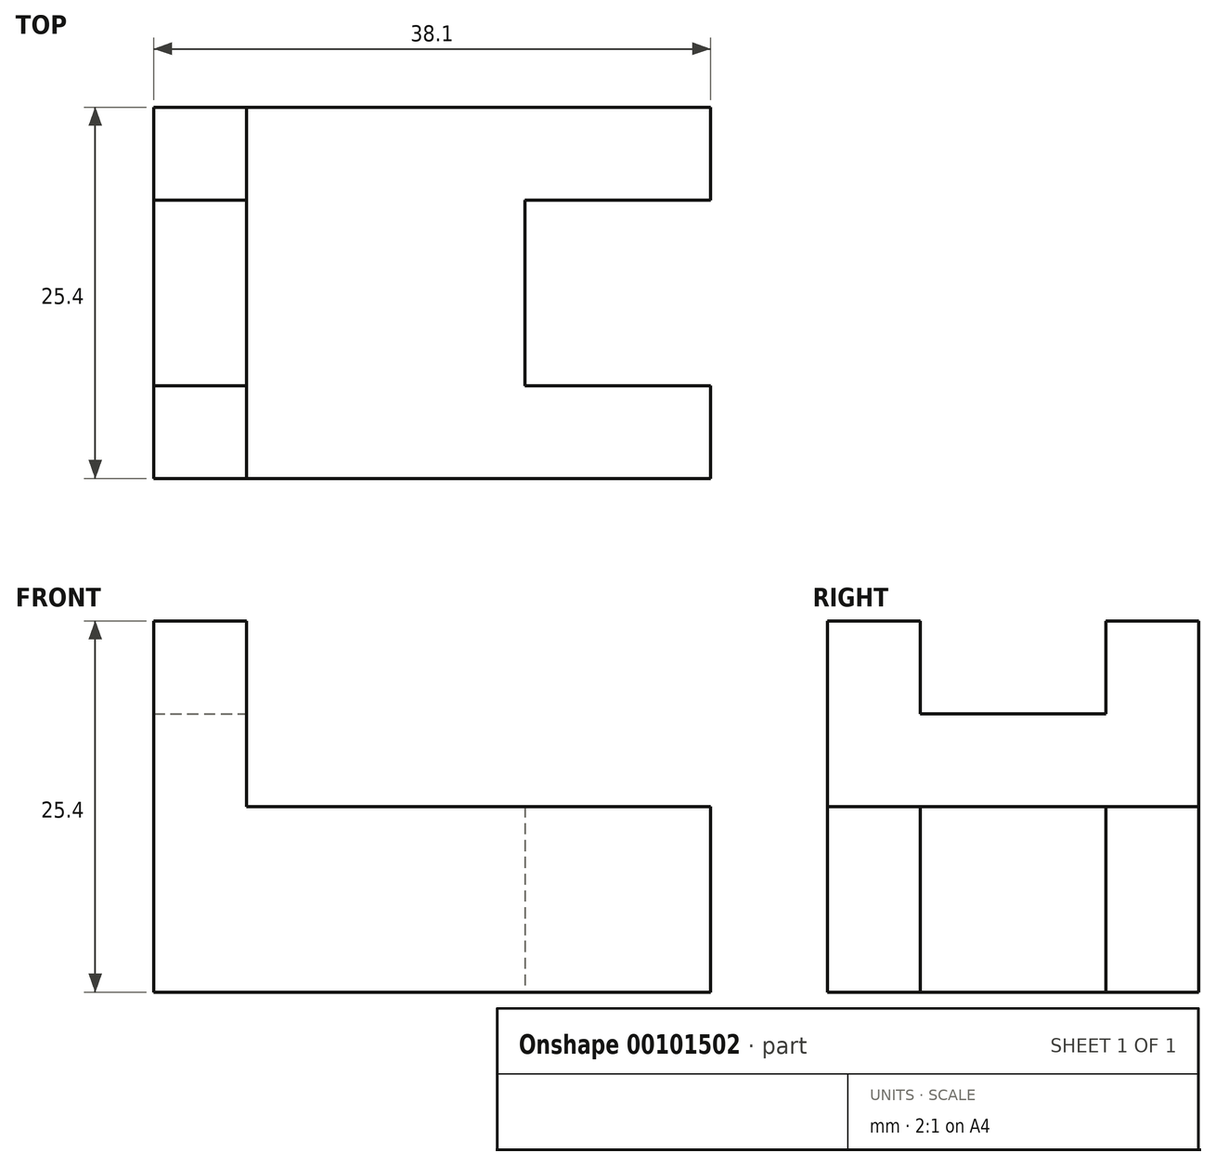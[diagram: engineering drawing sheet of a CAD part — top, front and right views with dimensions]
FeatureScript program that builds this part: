
annotation { "Feature Type Name" : "Feature", "Feature Type Description" : "" }
export const myFeature = defineFeature(function(context is Context, id is Id, definition is map)
    precondition{}
    {
        {
            var Q0;
            Q0=qCreatedBy(makeId("Front.planeOp"),FACE);
            var sketch = newSketch(context, id + "F0", { "sketchPlane" : qUnion([Q0])});
            skLineSegment(sketch, "E0", {"start": v(0, 0) * mm, "end": v(0, 25.4) * mm});
            skLineSegment(sketch, "E1", {"start": v(0, 25.4) * mm, "end": v(6.35, 25.4) * mm});
            skLineSegment(sketch, "E2", {"start": v(6.35, 25.4) * mm, "end": v(6.35, 12.7) * mm});
            skLineSegment(sketch, "E3", {"start": v(6.35, 12.7) * mm, "end": v(38.1, 12.7) * mm});
            skLineSegment(sketch, "E4", {"start": v(38.1, 12.7) * mm, "end": v(38.1, 0) * mm});
            skLineSegment(sketch, "E5", {"start": v(38.1, 0) * mm, "end": v(0, 0) * mm});
            skSolve(sketch);
        }
        {
            var Q0;
            Q0 = qSketchRegion(id + "F0", true);
            extrude(context, id + "F1", {"entities" : qUnion([Q0]), "endBound" : BoundingType.SYMMETRIC, "depth" : 25.4 * mm});
        }
        {
            var Q0;
            Q0=qCreatedBy(makeId("Front.planeOp"),FACE);
            var sketch = newSketch(context, id + "F2", { "sketchPlane" : qUnion([Q0])});
            skLineSegment(sketch, "E6", {"start": v(0, 19.05) * mm, "end": v(6.35, 19.05) * mm});
            skLineSegment(sketch, "E7", {"start": v(6.35, 25.4) * mm, "end": v(6.35, 19.05) * mm});
            skLineSegment(sketch, "E8", {"start": v(0, 25.4) * mm, "end": v(6.35, 25.4) * mm});
            skLineSegment(sketch, "E9", {"start": v(0, 19.05) * mm, "end": v(0, 25.4) * mm});
            skSolve(sketch);
        }
        {
            var Q0;
            Q0 = qSketchRegion(id + "F2", true);
            extrude(context, id + "F3", {"entities" : qUnion([Q0]), "operationType" : NewBodyOperationType.REMOVE, "endBound" : BoundingType.SYMMETRIC, "depth" : 12.7 * mm});
        }
        {
            var Q0;
            Q0=qCreatedBy(makeId("Front.planeOp"),FACE);
            var sketch = newSketch(context, id + "F4", { "sketchPlane" : qUnion([Q0])});
            skLineSegment(sketch, "E10.bottom", {"start": v(38.1, 12.7) * mm, "end": v(25.4, 12.7) * mm});
            skLineSegment(sketch, "E10.top", {"start": v(38.1, 0) * mm, "end": v(25.4, 0) * mm});
            skLineSegment(sketch, "E10.left", {"start": v(38.1, 12.7) * mm, "end": v(38.1, 0) * mm});
            skLineSegment(sketch, "E10.right", {"start": v(25.4, 12.7) * mm, "end": v(25.4, 0) * mm});
            skSolve(sketch);
        }
        {
            var Q0;
            Q0 = qSketchRegion(id + "F4", true);
            extrude(context, id + "F5", {"entities" : qUnion([Q0]), "operationType" : NewBodyOperationType.REMOVE, "endBound" : BoundingType.SYMMETRIC, "depth" : 12.7 * mm});
        }
    });
